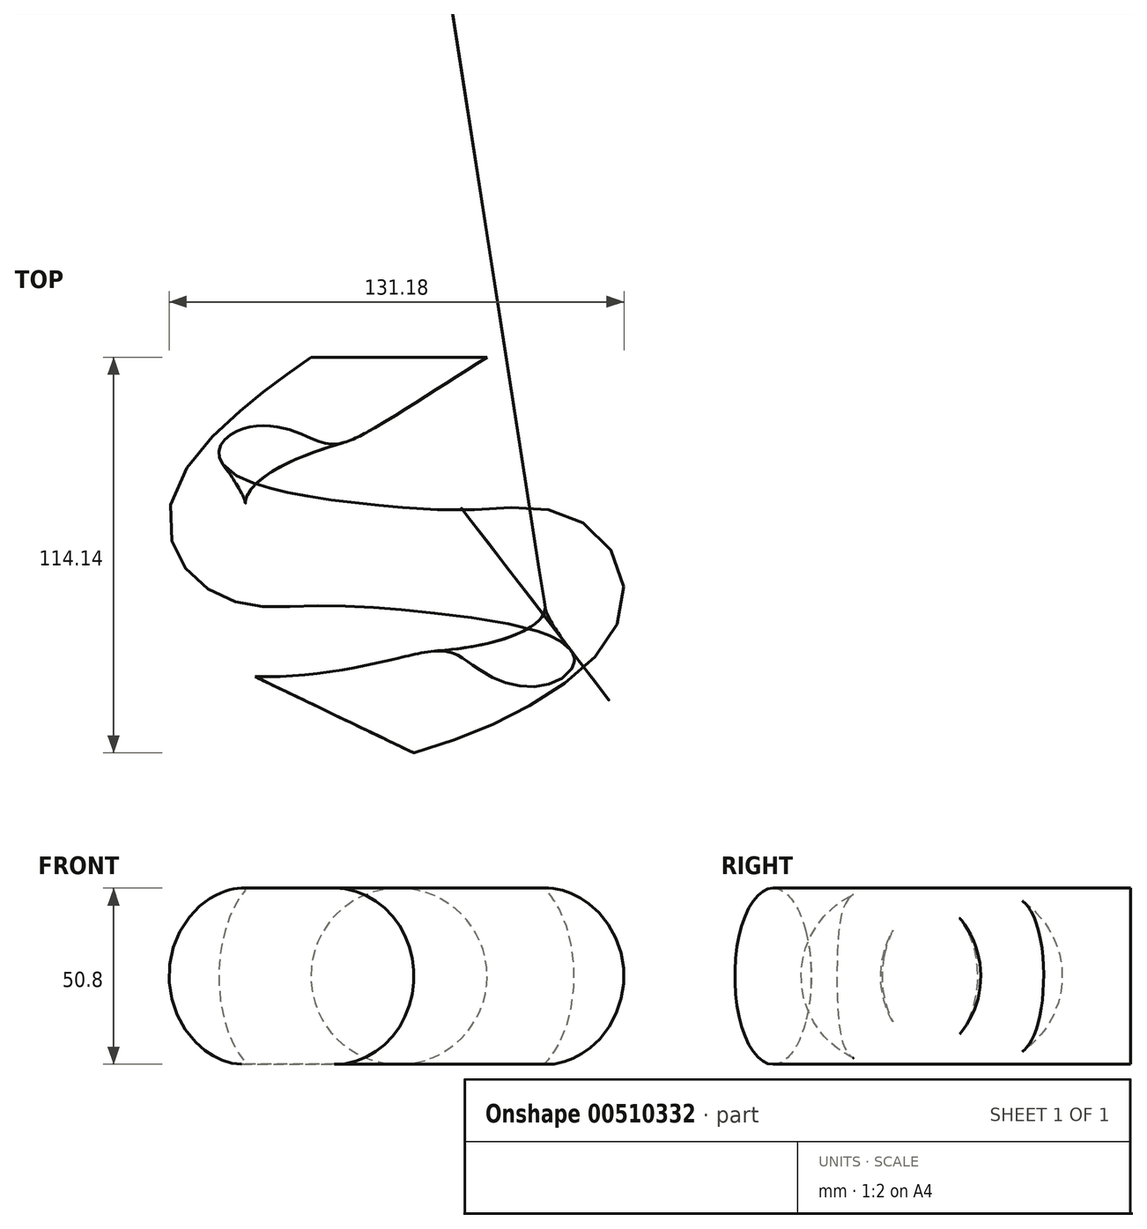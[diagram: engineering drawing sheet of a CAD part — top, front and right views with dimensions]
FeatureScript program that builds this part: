
annotation { "Feature Type Name" : "Feature", "Feature Type Description" : "" }
export const myFeature = defineFeature(function(context is Context, id is Id, definition is map)
    precondition{}
    {
        {
            var Q0;
            Q0=qCreatedBy(makeId("Front.planeOp"),FACE);
            var sketch = newSketch(context, id + "F0", { "sketchPlane" : qUnion([Q0])});
            skCircle(sketch, "E0", {"center": v(0, 0) * mm, "radius": 25.4 * mm});
            skSolve(sketch);
        }
        {
            var Q0;
            Q0=qCreatedBy(makeId("Top.planeOp"),FACE);
            var sketch = newSketch(context, id + "F1", { "sketchPlane" : qUnion([Q0])});
            skFitSpline(sketch, "E1", {"points": [v(0, 0) * mm, v(-43.13, -47.22) * mm, v(41.57, -68.4) * mm, v(-18.6, -103.14) * mm], "startDerivative": vector(-258.15, -172.93) * mm, "endDerivative": vector(-338.27, -48.43) * mm});
            skSolve(sketch);
        }
        {
            var Q0;
            Q0=makeQuery(id+"F0.imprint","IMPRINT",FACE,{"disambiguationData":[TD([[makeQuery(id+"F0.imprint","IMPRINT",EDGE,{"derivedFrom":sQuery(id+"F0.wireOp",EDGE,"E0")}),1.0]])]});
            var Q1;
            Q1=sQuery(id+"F1.wireOp",EDGE,"E1");
            sweep(context, id + "F2", {"profiles" : qUnion([Q0]), "path" : qUnion([Q1])});
        }
    });
